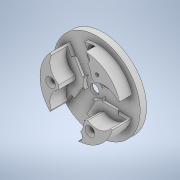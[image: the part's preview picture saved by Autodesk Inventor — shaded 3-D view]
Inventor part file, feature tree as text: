
AUTODESK INVENTOR PART (.ipt)
format: ipt  version: 2022 (Build 260153000, 153)  size: 486,400 bytes
history: native  units: mm
features: sketch x17, extrude x13, projected_geometry x10, hole x5, pattern_circular x2, chamfer x2
ambient origin geometry x8: Origin, YZ Plane, XZ Plane, XY Plane, X Axis, Y Axis, Z Axis, Center Point
bodies: Volumenkörper1 (feature_tree)
feature tree (49):
  extrude  "Extrusion1"  Depth=8.0mm TaperAngle=0.0deg
  extrude  "Extrusion2"  Depth=30.0mm TaperAngle=360.0deg
  extrude  "Extrusion3"  Depth=20.0mm
  extrude  "Extrusion4"  Depth=20.0mm
  extrude  "Extrusion21"  Depth=2.0mm TaperAngle=0.0deg
  extrude  "Extrusion6"  Depth=6.0mm
  pattern_circular  "Runde Anordnung1"  [2 undecoded]
  extrude  "Extrusion7"  Depth=0.5mm
  extrude  "Extrusion22"  Depth=10.0mm TaperAngle=0.0deg
  extrude  "Extrusion25"  Depth=10.0mm
  extrude  "Extrusion26"  TaperAngle=120.0deg  [1 undecoded]
  hole  "Bohrung8"  [1 undecoded]
  hole  "Bohrung9"  [1 undecoded]
  hole  "Bohrung10"  [1 undecoded]
  extrude  "Extrusion28"  Depth=0.5mm TaperAngle=30.0deg
  hole  "Bohrung11"  [1 undecoded]
  extrude  "Extrusion29"  Depth=1.8mm
  hole  "Bohrung12"  [1 undecoded]
  chamfer  "Fase1"  Distance=9.0mm
  pattern_circular  "Runde Anordnung7"  [2 undecoded]
  chamfer  "Fase2"  Distance=1.0mm Angle=45.0deg
  extrude  "Extrusion30"  Depth=0.5mm
  sketch  "Skizze1"  dims[d0=40.8mm d1=8.0mm d2=0.0mm]
  sketch  "Skizze2"  dims[d3=18.9mm d4=30.0mm d6=360.0deg]
  sketch  "Skizze3"  dims[d8=4.5mm d9=0.0mm d10=20.0mm]
  sketch  "Skizze4"  dims[d11=4.5mm d12=0.0mm d13=20.0mm]
  projected_geometry  "Projizierte Kontur1"
  projected_geometry  "Projizierte Kontur2"
  sketch  "Skizze6"  dims[d14=11.5mm d17=2.0mm d18=0.0mm]
  sketch  "Skizze7"  dims[d30=30.0mm d31=360.0deg d33=6.0mm]
  sketch  "Skizze25"  dims[d38=1.3mm d39=0.0mm]
  projected_geometry  "Projizierte Kontur6"
  sketch  "Skizze26"  dims[d40=11.0mm]
  projected_geometry  "Projizierte Kontur7"
  projected_geometry  "Projizierte Kontur8"
  projected_geometry  "Projizierte Kontur9"
  sketch  "Skizze33"  dims[d41=2.0mm d42=0.0mm]
  sketch  "Skizze34"  dims[d130=4.5mm d131=0.0mm]
  sketch  "Skizze38"  dims[d132=0.5mm d133=0.0mm]
  sketch  "Skizze40"  dims[d165=48.0mm]
  sketch  "Skizze41"  dims[d166=1.5mm d167=0.0mm]
  projected_geometry  "Projizierte Kontur13"
  projected_geometry  "Projizierte Kontur14"
  sketch  "Skizze42"  dims[d168=1.0mm]
  sketch  "Skizze45"  dims[d169=2.0mm d170=0.0mm]
  projected_geometry  "Projizierte Kontur15"
  projected_geometry  "Projizierte Kontur16"
  sketch  "Skizze46"  dims[d181=60.0deg]
  sketch  "Skizze47"  dims[d182=1.8mm d183=6.0mm d184=4.0mm d185=2.0mm d186=90.0deg d187=6.3mm d188=20.594885mm d190=35.0mm d191=6.0mm d192=6.0mm d193=6.0mm d194=12.0mm d195=90.0deg d196=60.0mm d197=0.0mm d200=36.0mm d201=3.2mm d202=6.0mm d203=5.2mm d204=9.0mm d205=90.0deg d206=60.0mm d207=0.0mm d208=10.0mm d209=0.0mm d210=10.0mm d211=120.0deg d212=2.5mm d213=5.0mm d214=6.0mm d215=4.0mm d216=2.0mm d217=90.0deg d218=80.0mm d219=0.0mm d224=4.0mm d225=0.0mm d226=14.5mm d227=2.3mm d228=6.0mm d229=4.0mm d230=2.0mm d231=90.0deg d232=6.3mm d233=20.594885mm d234=1.5mm d235=2.0mm d236=30.0deg d237=20.0mm d238=120.0deg d240=1.8mm d241=1.8mm d242=9.0mm d243=9.0mm d244=1.0mm d245=2.0mm d246=45.0deg d247=6.5mm d248=6.5mm d249=0.5mm d250=0.0mm d16=0.5mm d19=0.872665mm d20=0.872665mm d21=0.5mm d22=0.872665mm d52=0.5mm d53=0.872665mm d54=0.5mm d55=0.872665mm d75=0.5mm d76=0.872665mm d77=0.5mm d78=0.872665mm d93=1.0mm d94=1.0mm d95=1.0mm d96=0.15mm d97=0.25mm d98=0.375mm d99=14.3117mm d100=0.75mm d101=20.594885mm d102=0.0625mm d103=0.75mm d104=0.375mm d134=0.5mm d135=0.872665mm d136=0.5mm d137=0.872665mm]
note: 10 required parameter values undecoded (feature->parameter linkage not recoverable at this tier; creation-order binding heuristic only, values carry confidence <= 0.55)
